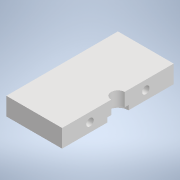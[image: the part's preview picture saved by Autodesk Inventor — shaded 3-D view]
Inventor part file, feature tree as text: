
AUTODESK INVENTOR PART (.ipt)
format: ipt  version: 2020 (Build 240168000, 168)  size: 145,408 bytes
history: native  units: mm
features: sketch x5, extrude x4, hole x1
ambient origin geometry x8: Origin, YZ Plane, XZ Plane, XY Plane, X Axis, Y Axis, Z Axis, Center Point
bodies: Solido1 (feature_tree)
feature tree (10):
  extrude  "Estrusione1"  Depth=50.0mm
  extrude  "Estrusione2"  Depth=16.0mm TaperAngle=0.0deg
  extrude  "Estrusione3"  Depth=19.0mm
  hole  "Foro1"  [1 undecoded]
  extrude  "Estrusione4"  Depth=12.0mm
  sketch  "Schizzo1"
  sketch  "Schizzo2"
  sketch  "Schizzo4"
  sketch  "Schizzo5"
  sketch  "Schizzo6"
note: 1 required parameter value undecoded (feature->parameter linkage not recoverable at this tier; creation-order binding heuristic only, values carry confidence <= 0.55)
